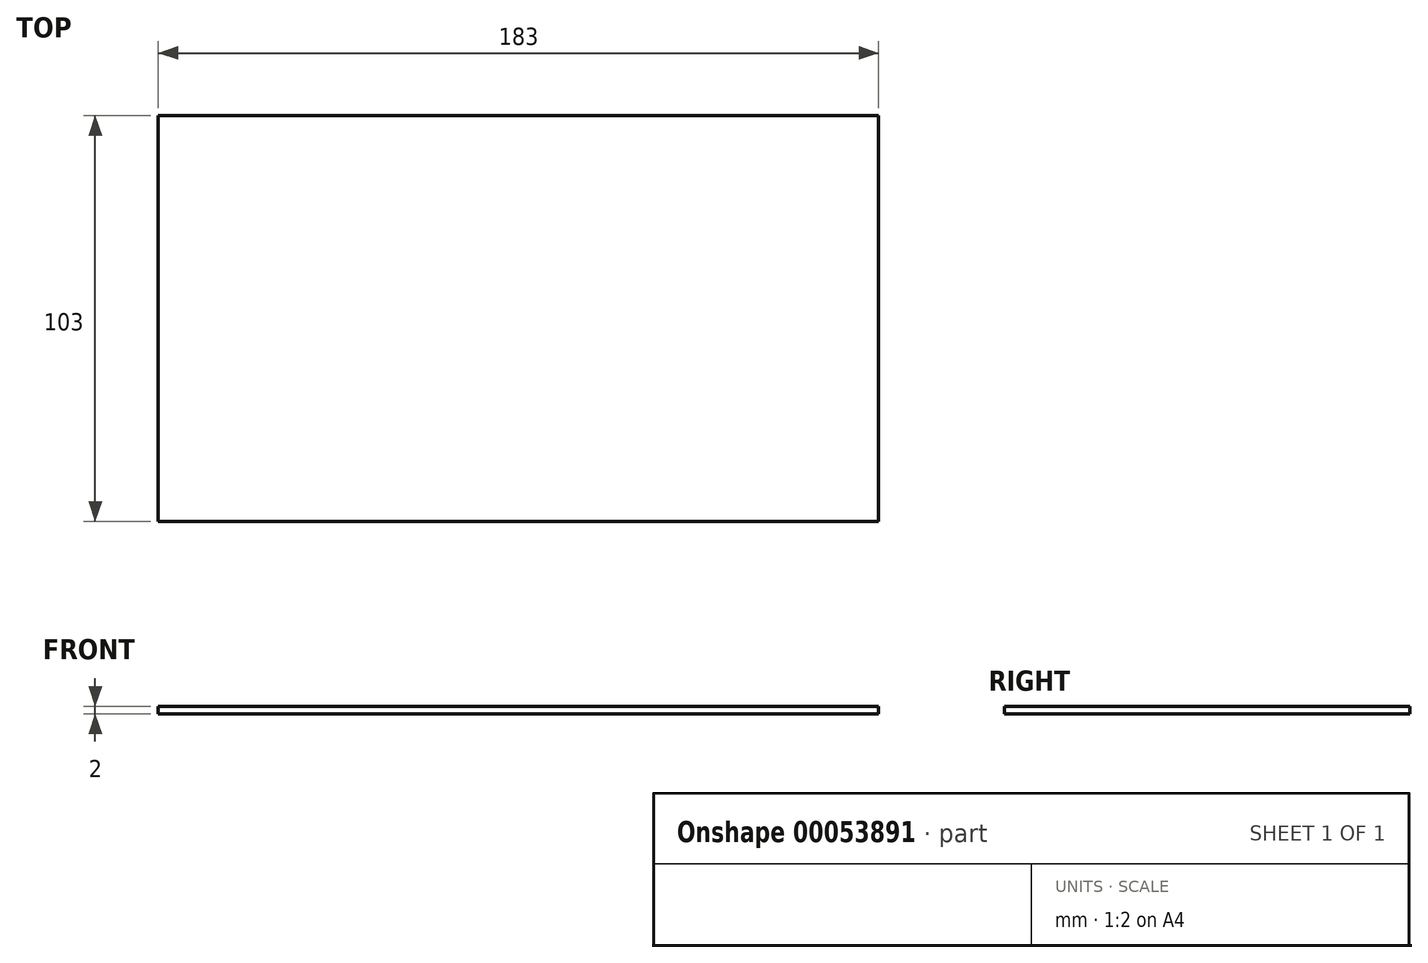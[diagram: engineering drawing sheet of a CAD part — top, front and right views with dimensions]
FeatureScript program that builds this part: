
annotation { "Feature Type Name" : "Feature", "Feature Type Description" : "" }
export const myFeature = defineFeature(function(context is Context, id is Id, definition is map)
    precondition{}
    {
        {
            var Q0;
            Q0=qCreatedBy(makeId("Top.planeOp"),FACE);
            var sketch = newSketch(context, id + "F0", { "sketchPlane" : qUnion([Q0])});
            skLineSegment(sketch, "E0.bottom", {"start": v(0, 0) * mm, "end": v(183, 0) * mm});
            skLineSegment(sketch, "E0.top", {"start": v(0, -103) * mm, "end": v(183, -103) * mm});
            skLineSegment(sketch, "E0.left", {"start": v(0, 0) * mm, "end": v(0, -103) * mm});
            skLineSegment(sketch, "E0.right", {"start": v(183, 0) * mm, "end": v(183, -103) * mm});
            skSolve(sketch);
        }
        {
            var Q0;
            Q0 = qSketchRegion(id + "F0", true);
            extrude(context, id + "F1", {"entities" : qUnion([Q0]), "depth" : 2 * mm});
        }
    });
